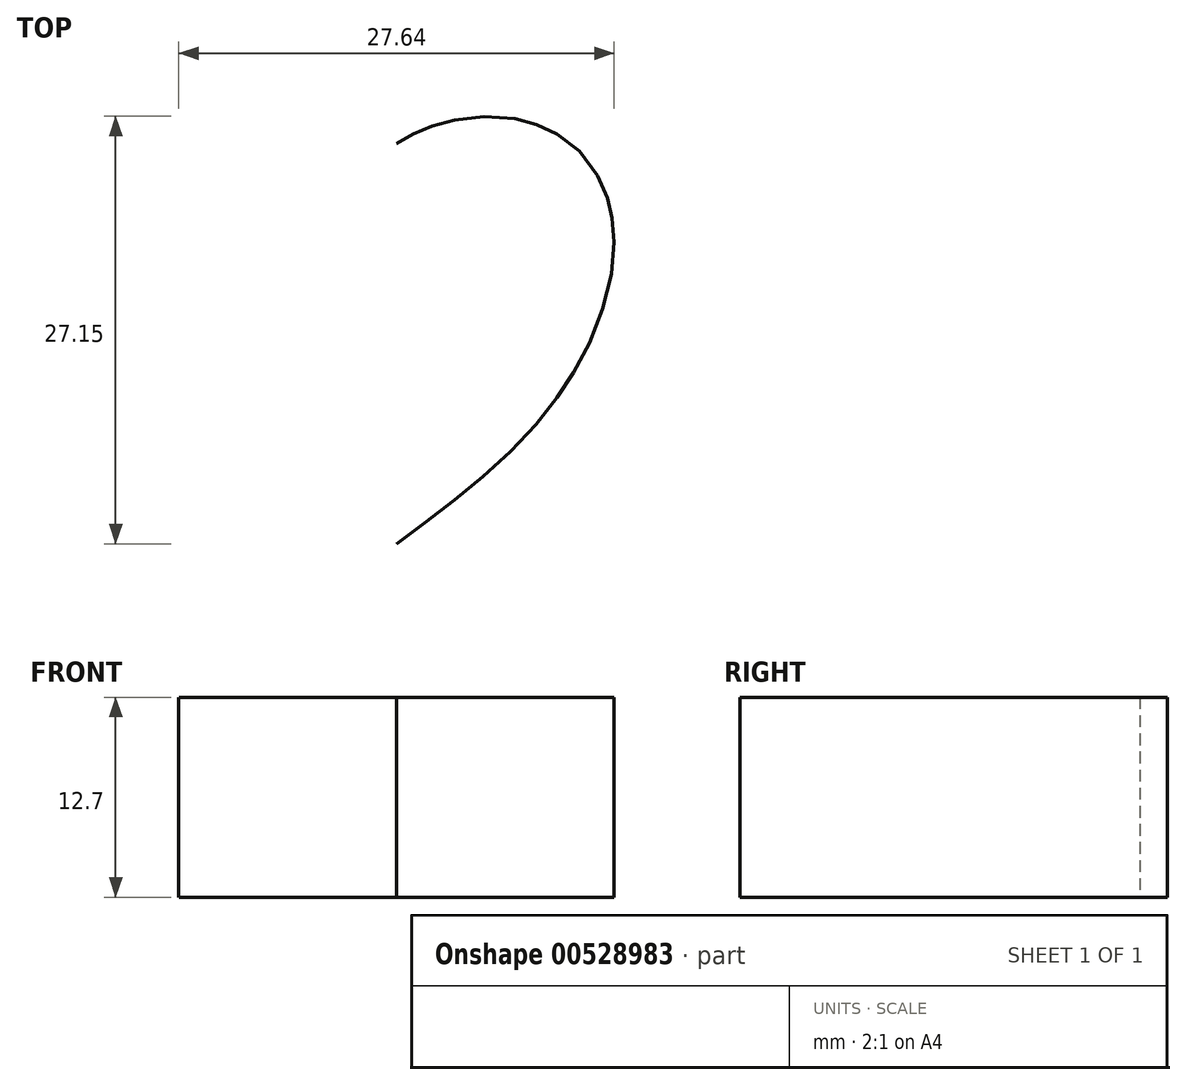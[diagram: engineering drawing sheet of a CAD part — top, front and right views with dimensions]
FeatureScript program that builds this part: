
annotation { "Feature Type Name" : "Feature", "Feature Type Description" : "" }
export const myFeature = defineFeature(function(context is Context, id is Id, definition is map)
    precondition{}
    {
        {
            var Q0;
            Q0=qCreatedBy(makeId("Top.planeOp"),FACE);
            var sketch = newSketch(context, id + "F0", { "sketchPlane" : qUnion([Q0])});
            skFitSpline(sketch, "E0.0", {"points": [v(3.17, 4.53) * mm, v(2.94, 4.77) * mm, v(2.48, 5.27) * mm, v(1.7, 6.04) * mm, v(0.99, 6.68) * mm, v(0.35, 7.16) * mm, v(-0.16, 7.51) * mm, v(-0.62, 7.78) * mm, v(-1, 7.99) * mm, v(-1.4, 8.18) * mm, v(-1.93, 8.4) * mm, v(-2.57, 8.62) * mm, v(-3.23, 8.8) * mm, v(-4.13, 9) * mm, v(-5.29, 9.13) * mm, v(-6.7, 9.12) * mm, v(-7.77, 8.95) * mm, v(-8.46, 8.76) * mm, v(-8.92, 8.6) * mm, v(-9.49, 8.38) * mm, v(-10.13, 8.05) * mm, v(-10.94, 7.52) * mm, v(-11.85, 6.72) * mm, v(-12.59, 5.73) * mm, v(-13.06, 4.85) * mm, v(-13.34, 4.14) * mm, v(-13.53, 3.52) * mm, v(-13.64, 3.01) * mm, v(-13.72, 2.5) * mm, v(-13.8, 1.84) * mm, v(-13.81, 0.78) * mm, v(-13.7, -0.56) * mm, v(-13.36, -2.2) * mm, v(-12.83, -3.85) * mm, v(-12.14, -5.48) * mm, v(-11.44, -6.8) * mm, v(-10.8, -7.84) * mm, v(-10.12, -8.84) * mm, v(-9.2, -10.04) * mm, v(-7.98, -11.4) * mm, v(-6.69, -12.67) * mm, v(-5.33, -13.88) * mm, v(-3.92, -15.04) * mm, v(-2.48, -16.16) * mm, v(-1.02, -17.26) * mm, v(0.2, -18.15) * mm, v(1.17, -18.86) * mm, v(1.66, -19.21) * mm, v(1.9, -19.39) * mm]});
            skFitSpline(sketch, "E0.1", {"points": [v(-3.17, 4.53) * mm, v(-2.94, 4.77) * mm, v(-2.48, 5.27) * mm, v(-1.7, 6.04) * mm, v(-0.99, 6.68) * mm, v(-0.35, 7.16) * mm, v(0.16, 7.51) * mm, v(0.62, 7.78) * mm, v(1, 7.99) * mm, v(1.4, 8.18) * mm, v(1.93, 8.4) * mm, v(2.57, 8.62) * mm, v(3.23, 8.8) * mm, v(4.13, 9) * mm, v(5.29, 9.13) * mm, v(6.7, 9.12) * mm, v(7.77, 8.95) * mm, v(8.46, 8.76) * mm, v(8.92, 8.6) * mm, v(9.49, 8.38) * mm, v(10.13, 8.05) * mm, v(10.94, 7.52) * mm, v(11.85, 6.72) * mm, v(12.59, 5.73) * mm, v(13.06, 4.85) * mm, v(13.34, 4.14) * mm, v(13.53, 3.52) * mm, v(13.64, 3.01) * mm, v(13.72, 2.5) * mm, v(13.8, 1.84) * mm, v(13.81, 0.78) * mm, v(13.7, -0.56) * mm, v(13.36, -2.2) * mm, v(12.83, -3.85) * mm, v(12.14, -5.48) * mm, v(11.44, -6.8) * mm, v(10.8, -7.84) * mm, v(10.12, -8.84) * mm, v(9.2, -10.04) * mm, v(7.98, -11.4) * mm, v(6.69, -12.67) * mm, v(5.33, -13.88) * mm, v(3.92, -15.04) * mm, v(2.48, -16.16) * mm, v(1.02, -17.26) * mm, v(-0.2, -18.15) * mm, v(-1.17, -18.86) * mm, v(-1.66, -19.21) * mm, v(-1.9, -19.39) * mm]});
            skSolve(sketch);
        }
        {
            var Q0;
            Q0=makeQuery(id+"F0.imprint","IMPRINT",FACE,{"disambiguationData":[TD([[makeQuery(id+"F0.imprint","IMPRINT",EDGE,{"derivedFrom":sQuery(id+"F0.wireOp",EDGE,"E0.0")}),1.0]])]});
            extrude(context, id + "F1", {"entities" : qUnion([Q0]), "depth" : 12.7 * mm, "offsetDistance" : 25.4 * mm});
        }
    });
